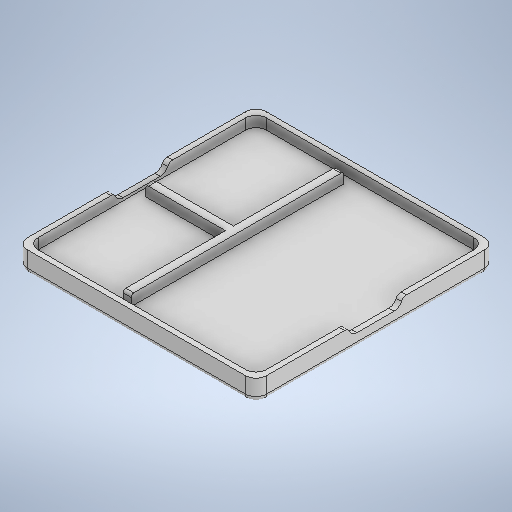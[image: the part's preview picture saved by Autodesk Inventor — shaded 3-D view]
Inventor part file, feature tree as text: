
AUTODESK INVENTOR PART (.ipt)
format: ipt  version: 2025 (Build 290162000, 162)  size: 724,992 bytes
history: native  units: mm
features: extrude x4, fillet x4, sketch x3, other x2
ambient origin geometry x8: Origin, YZ Plane, XZ Plane, XY Plane, X Axis, Y Axis, Z Axis, Center Point
bodies: Body1 (feature_tree)
feature tree (13):
  other  "ソリッド1"
  extrude  "押し出し1"  Depth=45.0mm
  extrude  "押し出し2"  Depth=45.0mm
  extrude  "押し出し3"  Depth=4.0mm TaperAngle=0.0deg
  fillet  "フィレット1"  Radius=2.0mm
  fillet  "フィレット2"  Radius=1.0mm
  extrude  "押し出し4"  Depth=1.0mm
  fillet  "フィレット3"  Radius=1.0mm
  fillet  "フィレット4"  Radius=1.0mm
  other  "底面スケッチ"
  sketch  "スケッチ2"
  sketch  "スケッチ3"
  sketch  "スケッチ4"
